# Revit family: Pump_Commercial-Submersible_Dewatering-Zoeller-M212
name_source: partatom
category: Mechanical Equipment
revit_build: Autodesk Revit 2014 (Build: 20130308_1515(x64)
units: mm (PartAtom-declared; Revit-internal decimal feet)

## types (1)
- M212
    Amps = 7 A
    Apparent Load = 759 VA
    Assembly Code = D2090
    Auto On/Off Points = 11 1/2” (29 cm) / 5 1/4” (13 cm)
    Base = Engineered Plastic
    Cooling = Oil Filled
    Cord Length = 120"
    Cord Type = UL listed 3-prong plug
    Default Elevation = 0"
    Description = Submersible Pump for Sewage, Effluent and Dewatering.
    Discharge Diameter = 2"
    Discharge Height = 5 3/4"
    Flow Rate = 82 GPM
    Gasket = NBR
    Hardware = Stainless Steel
    Height = 15 1/8"
    Hertz = 60
    Horse Power = 1/2
    Impeller = Engineered Plastic
    Impeller Type = Non-Clogging Vortex
    Installation Type = Floor Mounted
    Insulation = Class B
    Length = 9 27/32"
    Lower Bearing = Ball Bearing
    Manufacturer = Zoeller
    Max Flow Rate = 82 GPM (310 LPM)
    Max. Head = 19.5' (5.9 m)
    Max. Operating Temp. = 104° F (40° C)
    Mechanical Seals = Carbon and Ceramic
    Model = M212
    Motor Housing = Cast Iron
    Motor Protection = Auto reset thermal overload (1 Ph)
    Motor Shaft = SUS420J2 Stainless Steel
    Operation = Automatic
    Phase = 1 Ph
    Price = Prices may vary. Please consult Manufacturer Representative for most up-to-date price list.
    Product Documentation Link = http://cdn.qleapahead.com
    Product Page URL = http://www.zoellerpumps.com
    Pump Housing = Engineered Plastic
    RPM = 3400
    Shipping Weight = 20 lb
    Solid Handling = 2in (50 mm) spherical solids
    Type = Permanent Split Capacitor
    URL = http://www.zoellerpumps.com
    Upper Bearing = Ball Bearing
    Voltage = 115 V
    Warranty Information = 36 Months (Limited)
    Waste Connection = Yes
    Width = 7 11/16"

## geometry (parser evidence)
native form markers: Sweep x3
no freeform markers — native parametric forms only
